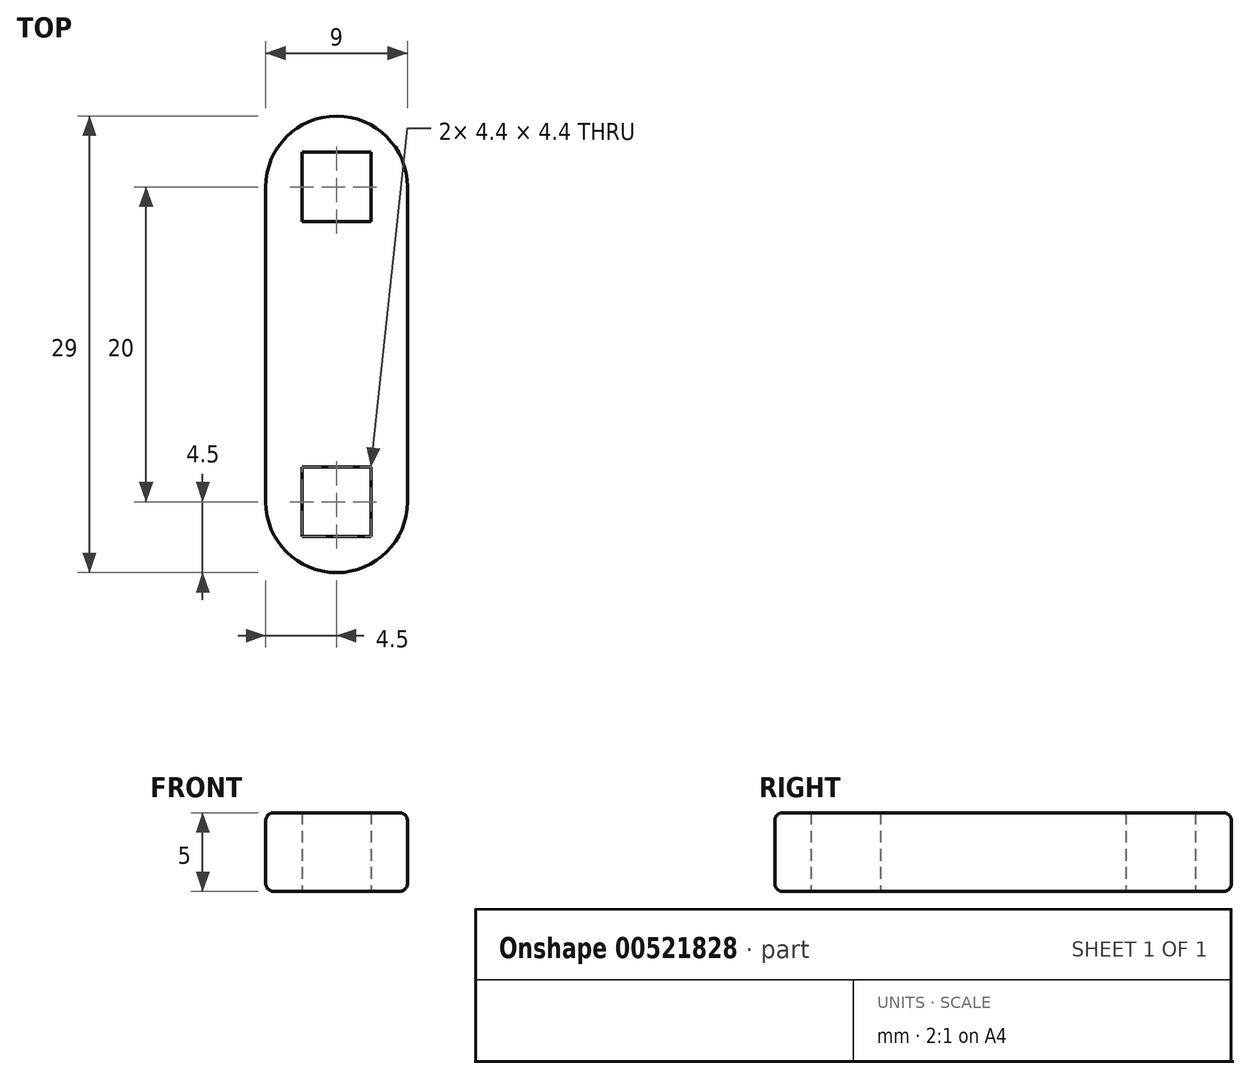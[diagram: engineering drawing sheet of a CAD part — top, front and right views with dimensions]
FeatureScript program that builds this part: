
annotation { "Feature Type Name" : "Feature", "Feature Type Description" : "" }
export const myFeature = defineFeature(function(context is Context, id is Id, definition is map)
    precondition{}
    {
        {
            var Q0;
            Q0=qCreatedBy(makeId("Top.planeOp"),FACE);
            var sketch = newSketch(context, id + "F0", { "sketchPlane" : qUnion([Q0])});
            skLineSegment(sketch, "E0.bottom", {"start": v(4.5, 14.5) * mm, "end": v(-4.5, 14.5) * mm});
            skLineSegment(sketch, "E0.top", {"start": v(4.5, -14.5) * mm, "end": v(-4.5, -14.5) * mm});
            skLineSegment(sketch, "E0.left", {"start": v(4.5, 14.5) * mm, "end": v(4.5, -14.5) * mm});
            skLineSegment(sketch, "E0.right", {"start": v(-4.5, 14.5) * mm, "end": v(-4.5, -14.5) * mm});
            skPoint(sketch, "E0.middle", {"position": v(0, 0) * mm});
            skLineSegment(sketch, "E1", {"start": v(0, -14.5) * mm, "end": v(0, -10) * mm});
            skPoint(sketch, "E1.endSnap0", {"position": v(0, -14.5) * mm});
            skLineSegment(sketch, "E2", {"start": v(0, 14.5) * mm, "end": v(0, 10) * mm});
            skPoint(sketch, "E2.endSnap0", {"position": v(0, 14.5) * mm});
            skLineSegment(sketch, "E3.bottom", {"start": v(-2.2, 7.8) * mm, "end": v(2.2, 7.8) * mm});
            skLineSegment(sketch, "E3.top", {"start": v(-2.2, 12.2) * mm, "end": v(2.2, 12.2) * mm});
            skLineSegment(sketch, "E3.left", {"start": v(-2.2, 7.8) * mm, "end": v(-2.2, 12.2) * mm});
            skLineSegment(sketch, "E3.right", {"start": v(2.2, 7.8) * mm, "end": v(2.2, 12.2) * mm});
            skPoint(sketch, "E3.middle", {"position": v(0, 10) * mm});
            skLineSegment(sketch, "E4.bottom", {"start": v(2.2, -7.8) * mm, "end": v(-2.2, -7.8) * mm});
            skLineSegment(sketch, "E4.top", {"start": v(2.2, -12.2) * mm, "end": v(-2.2, -12.2) * mm});
            skLineSegment(sketch, "E4.left", {"start": v(2.2, -7.8) * mm, "end": v(2.2, -12.2) * mm});
            skLineSegment(sketch, "E4.right", {"start": v(-2.2, -7.8) * mm, "end": v(-2.2, -12.2) * mm});
            skPoint(sketch, "E4.middle", {"position": v(0, -10) * mm});
            skSolve(sketch);
        }
        {
            var Q0;
            {var subQ5=sQuery(id+"F0.wireOp",EDGE,"E0.left");Q0=makeQuery(id+"F0.imprint","IMPRINT",FACE,{"disambiguationData":[TD([[makeQuery(id+"F0.imprint","IMPRINT",EDGE,{"derivedFrom":subQ5}),-1.0]])]});}
            extrude(context, id + "F1", {"entities" : qUnion([Q0]), "depth" : 5 * mm, "offsetDistance" : 25 * mm});
        }
        {
            var Q0;
            Q0=makeQuery(id+"F1.opExtrude","SWEPT_EDGE",EDGE,{"disambiguationData":[OSD([sQuery(id+"F0.wireOp",EDGE,"E0.bottom"),sQuery(id+"F0.wireOp",EDGE,"E0.right")])]});
            var Q1;
            Q1=makeQuery(id+"F1.opExtrude","SWEPT_EDGE",EDGE,{"disambiguationData":[OSD([sQuery(id+"F0.wireOp",EDGE,"E0.bottom"),sQuery(id+"F0.wireOp",EDGE,"E0.left")])]});
            var Q2;
            Q2=makeQuery(id+"F1.opExtrude","SWEPT_EDGE",EDGE,{"disambiguationData":[OSD([sQuery(id+"F0.wireOp",EDGE,"E0.top"),sQuery(id+"F0.wireOp",EDGE,"E0.left")])]});
            var Q3;
            Q3=makeQuery(id+"F1.opExtrude","SWEPT_EDGE",EDGE,{"disambiguationData":[OSD([sQuery(id+"F0.wireOp",EDGE,"E0.top"),sQuery(id+"F0.wireOp",EDGE,"E0.right")])]});
            fillet(context, id + "F2", {"entities" : qUnion([Q0, Q1, Q2, Q3]), "radius" : 4.5 * mm, "tangentPropagation" : true, "allowEdgeOverflow" : false});
        }
        {
            var Q0;
            Q0=makeQuery(id+"F1.opExtrude","CAP_EDGE",EDGE,{"disambiguationData":[OSD([sQuery(id+"F0.wireOp",EDGE,"E0.right")])],"isStart":false});
            var Q1;
            Q1=makeQuery(id+"F1.opExtrude","CAP_EDGE",EDGE,{"disambiguationData":[OSD([sQuery(id+"F0.wireOp",EDGE,"E0.right")])],"isStart":true});
            fillet(context, id + "F3", {"entities" : qUnion([Q0, Q1]), "radius" : .5 * mm, "tangentPropagation" : true, "allowEdgeOverflow" : false});
        }
    });
